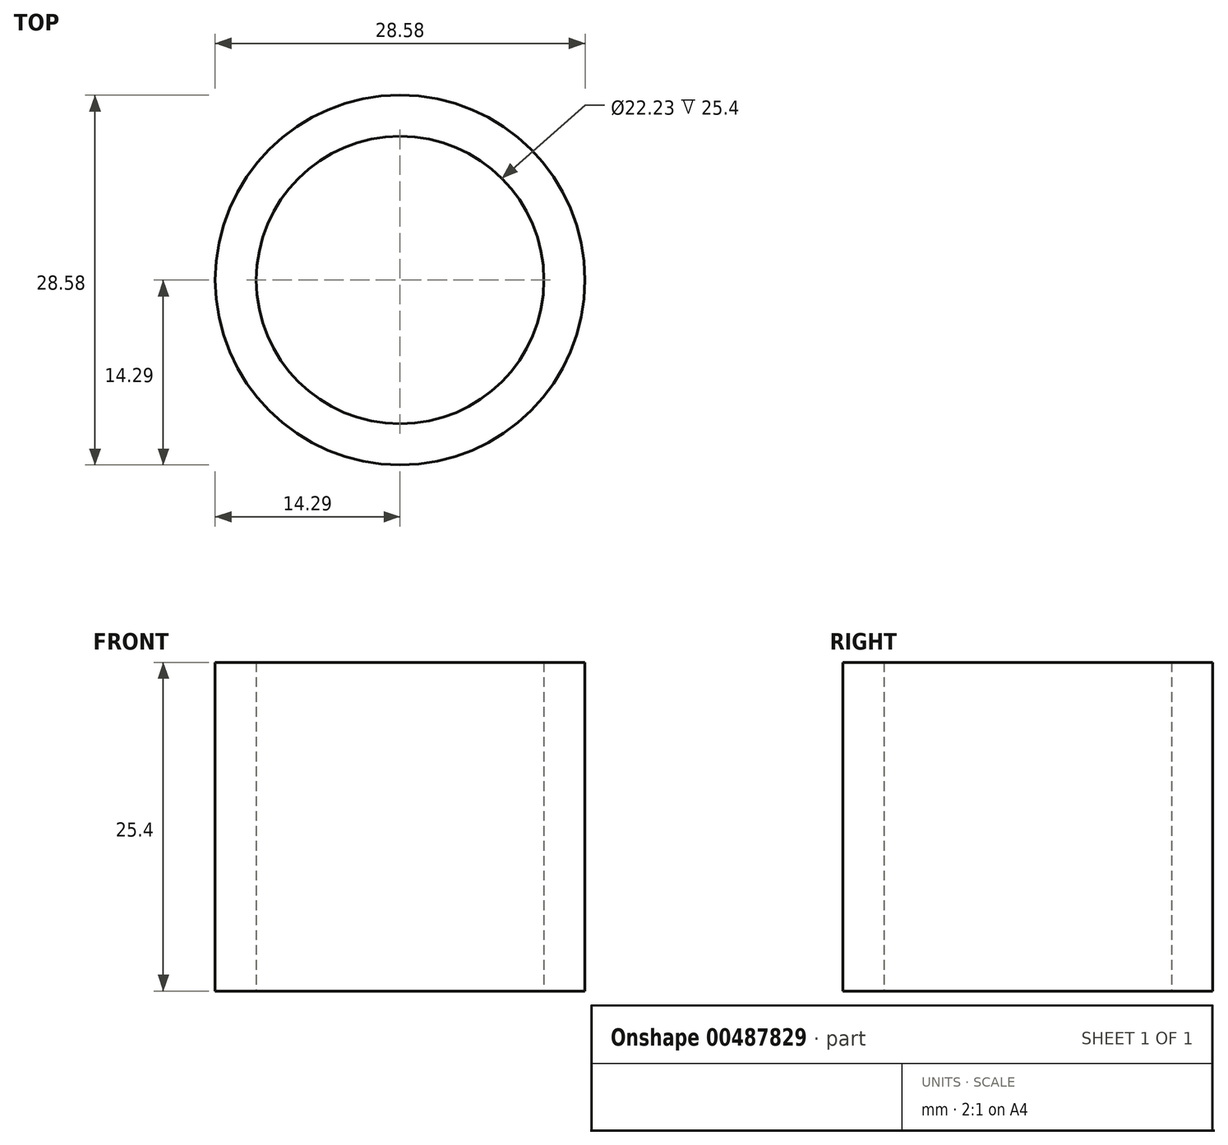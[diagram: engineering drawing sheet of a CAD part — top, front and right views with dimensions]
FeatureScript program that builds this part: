
annotation { "Feature Type Name" : "Feature", "Feature Type Description" : "" }
export const myFeature = defineFeature(function(context is Context, id is Id, definition is map)
    precondition{}
    {
        {
            var Q0;
            Q0=qCreatedBy(makeId("Top.planeOp"),FACE);
            var sketch = newSketch(context, id + "F0", { "sketchPlane" : qUnion([Q0])});
            skCircle(sketch, "E0", {"center": v(0, 0) * mm, "radius": 11.11 * mm});
            skCircle(sketch, "E1", {"center": v(0, 0) * mm, "radius": 14.29 * mm});
            skSolve(sketch);
        }
        {
            var Q0;
            Q0=makeQuery(id+"F0.imprint","IMPRINT",FACE,{"disambiguationData":[TD([[makeQuery(id+"F0.imprint","IMPRINT",EDGE,{"derivedFrom":sQuery(id+"F0.wireOp",EDGE,"E0")}),-1.0]])]});
            extrude(context, id + "F1", {"entities" : qUnion([Q0]), "depth" : 25.4 * mm});
        }
    });
